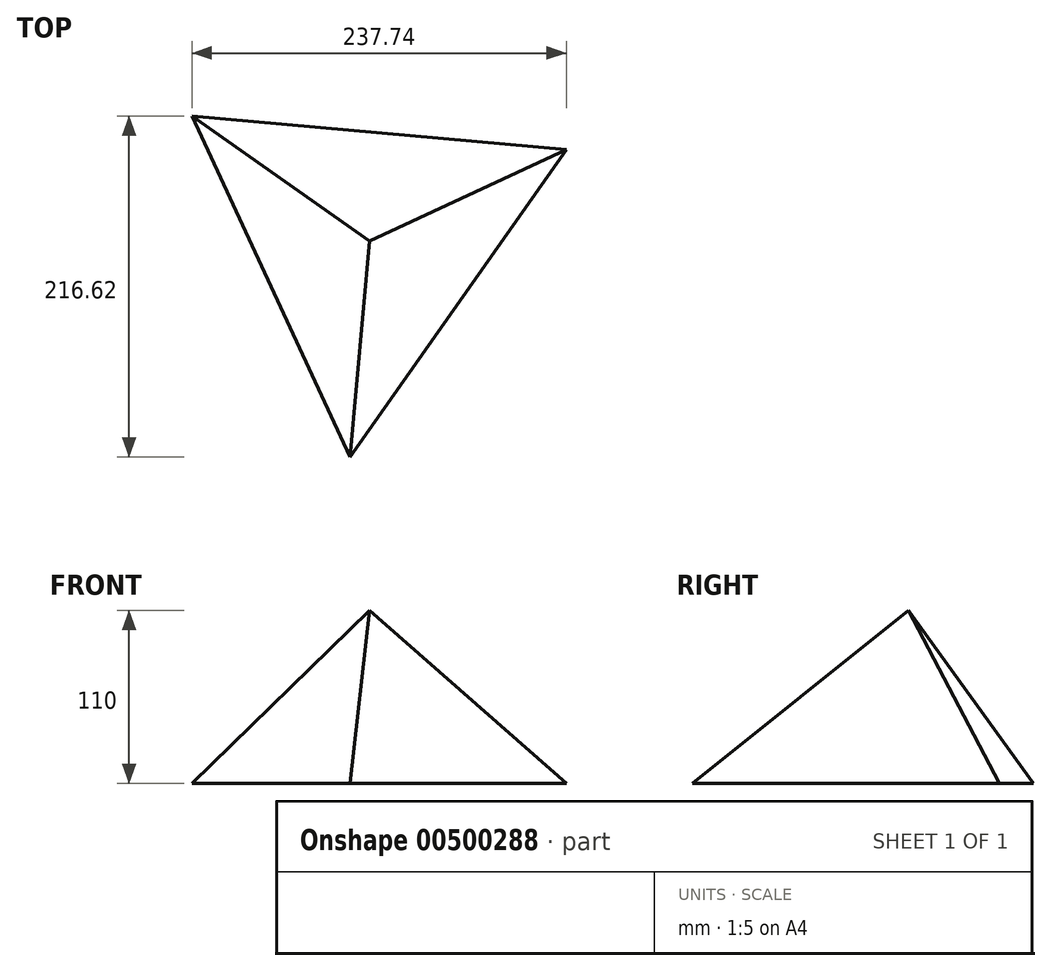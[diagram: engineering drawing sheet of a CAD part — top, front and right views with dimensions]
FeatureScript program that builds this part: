
annotation { "Feature Type Name" : "Feature", "Feature Type Description" : "" }
export const myFeature = defineFeature(function(context is Context, id is Id, definition is map)
    precondition{}
    {
        {
            var Q0;
            Q0=qCreatedBy(makeId("Top.planeOp"),FACE);
            var sketch = newSketch(context, id + "F0", { "sketchPlane" : qUnion([Q0])});
            skCircle(sketch, "E0.cCircle", {"center": v(0, 0) * mm, "radius": 137.82 * mm, "construction": true});
            skLineSegment(sketch, "E0.0", {"start": v(-112.67, 79.36) * mm, "end": v(125.07, 57.9) * mm});
            skLineSegment(sketch, "E0.1", {"start": v(125.07, 57.9) * mm, "end": v(-12.4, -137.26) * mm});
            skLineSegment(sketch, "E0.2", {"start": v(-12.4, -137.26) * mm, "end": v(-112.67, 79.36) * mm});
            skSolve(sketch);
        }
        {
            var Q0;
            Q0=qCreatedBy(makeId("Top.planeOp"),FACE);
            cPlane(context, id + "F1", {"entities" : qUnion([Q0]), "cplaneType" : CPlaneType.OFFSET, "offset" : 110 * mm, "width" : 152.4 * mm, "height" : 152.4 * mm});
        }
        {
            var Q0;
            Q0=qCreatedBy(id+"F1.planeOp",FACE);
            var sketch = newSketch(context, id + "F2", { "sketchPlane" : qUnion([Q0])});
            skPoint(sketch, "E1", {"position": v(0, 0) * mm});
            skSolve(sketch);
        }
        {
            var Q0;
            Q0=sQuery(id+"F2.wireOp",VERTEX,"E1");
            var Q1;
            Q1=makeQuery(id+"F0.imprint","IMPRINT",FACE,{"disambiguationData":[TD([[makeQuery(id+"F0.imprint","IMPRINT",EDGE,{"derivedFrom":sQuery(id+"F0.wireOp",EDGE,"E0.0")}),-1.0]])]});
            loft(context, id + "F3", {"sheetProfilesArray" : [{ "sheetProfileEntities" : qUnion([Q0]) }, { "sheetProfileEntities" : qUnion([Q1]) }]});
        }
    });
